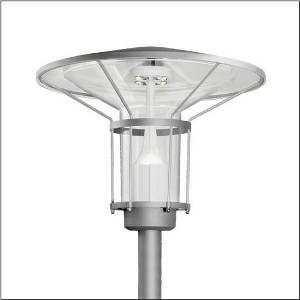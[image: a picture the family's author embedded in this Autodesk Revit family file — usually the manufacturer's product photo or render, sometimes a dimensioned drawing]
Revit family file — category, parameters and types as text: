
# Revit family: laterne_classic_iq___pl1_2s_5xa5245cf14h_6b83
name_source: partatom
category: Lighting Fixtures
units: mm (PartAtom-declared; Revit-internal decimal feet)

## family parameters
Cut with Voids When Loaded = No
Host = Face
Light Source = No
Part Type = Normal
Room Calculation Point = No
Round Connector Dimension = Use Diameter
Shared = No

## types (1)
- --- (1 x LED, 2670 lm, 23.9 W, 2200K)
    Apparent Load = 24 VA
    CIE Flux Codes = 21 60 93 97 100
    Color Rendering = 70
    Color Temperature = 2200K
    Default Elevation = 1800 mm
    Description = Lantern Classic iQ, mast luminaire, Module 540 iQ-SR, primary light control with 3 zone facetted reflector, of plastic, silver coated, highly specular, structured, primary optical cover: cover, of PMMA, transparent, light distribution: PL1.2s, light emission: direct distribution, primary light characteristic: symmetric, installation type: post-top, LED, High Power LED, rated luminous flux: 2.670lm, luminous efficacy: 112lm/W, light colour: 722, colour temperature: 2200K, control gear: iQ Street-Remote, control: pre-setting: logarithmic dimming characteristic, Street-Remote, Auto-Match, Temp-Guard, Lumen-Switch, Night-Set, Smart-Wire, Light-Fading, Desk-Remote (wireless, voltage-free reading and setting of iQ features in the workshop via application-optimized NFC function/RFID function), optimised constant luminous flux control (CLO 2.0), with terminal, 6-pole, max. 2.5mm², mains connection: 230..240V, AC, 50/60Hz, start of lifetime: 24W, end of service life: 26W, reduction: 12W, luminaire housing, upper part, of glass-fibre reinforced polyester, coated, Siteco® metallic grey (DB 702S), diameter: 750mm, height: 596mm, spigot size: d x l = 76 x 70mm (post-top) | with reducer (optional accessory) 60 x 70mm, mounting height: 3..5m, post-top mast mounting element, of diecast aluminium, coated, Siteco® metallic grey (DB 702S), Module 540 iQ-SR, traffic white (RAL 9016), equipment: standard, protection rating (complete): IP65, insulation class (complete): insulation class II (safety insulation), certification: CE, ENEC, VDE, packaging unit: 1 piece

Light Distribution: PL1.2s
    Height = 596 mm
    Lamp = 1 x LED
    Lamp Light Flux = 2670 lm
    Lamp Power = 23.9 W
    Lamp count = 1
    Length = 750 mm
    Luminous efficacy = 112 lm/W
    Manufacturer = Siteco
    ModVariant = No
    Model = 5XA5245CF14H
    Number of Poles = 1
    OnlyDefault = Yes
    Power Factor = 1
    Product Name = Laterne Classic iQ | PL1.2s
    Product group = mast luminaire | pylon top
    ProductGroupID = 6100
    Protection Class = Protection class II
    Protection Degree = IP 65
    RLX_Detail_Level = 1
    RLX_Emergency_Light_Flux = 0 lm
    RLX_Emergency_Type = 0
    RLX_Emergency_Type_DB = No
    RlxData = <blob elided: 37869 chars, md5=3f5e0a40>
    Socket = socket
    Standby Power = 0 W
    System Light Flux = 2670 lm
    System Power = 24 W
    Type Comments = factory setting: luminous flux: 100 % | dim-lin: 254 | 499 mA
    Type Image = l_1006052.jpg
    URL = http://relux.com
    VarID = @adj_167255
    Voltage = 0 V
    Weight = 0.00 kg
    Width = 0 mm  [stored 0 ft]

note: [stored X ft] marks values corroborated as IEEE doubles in the binary element streams (Revit-internal decimal feet)

## geometry (parser evidence)
native form markers: Blend x4, Sweep x11
no freeform markers — native parametric forms only
